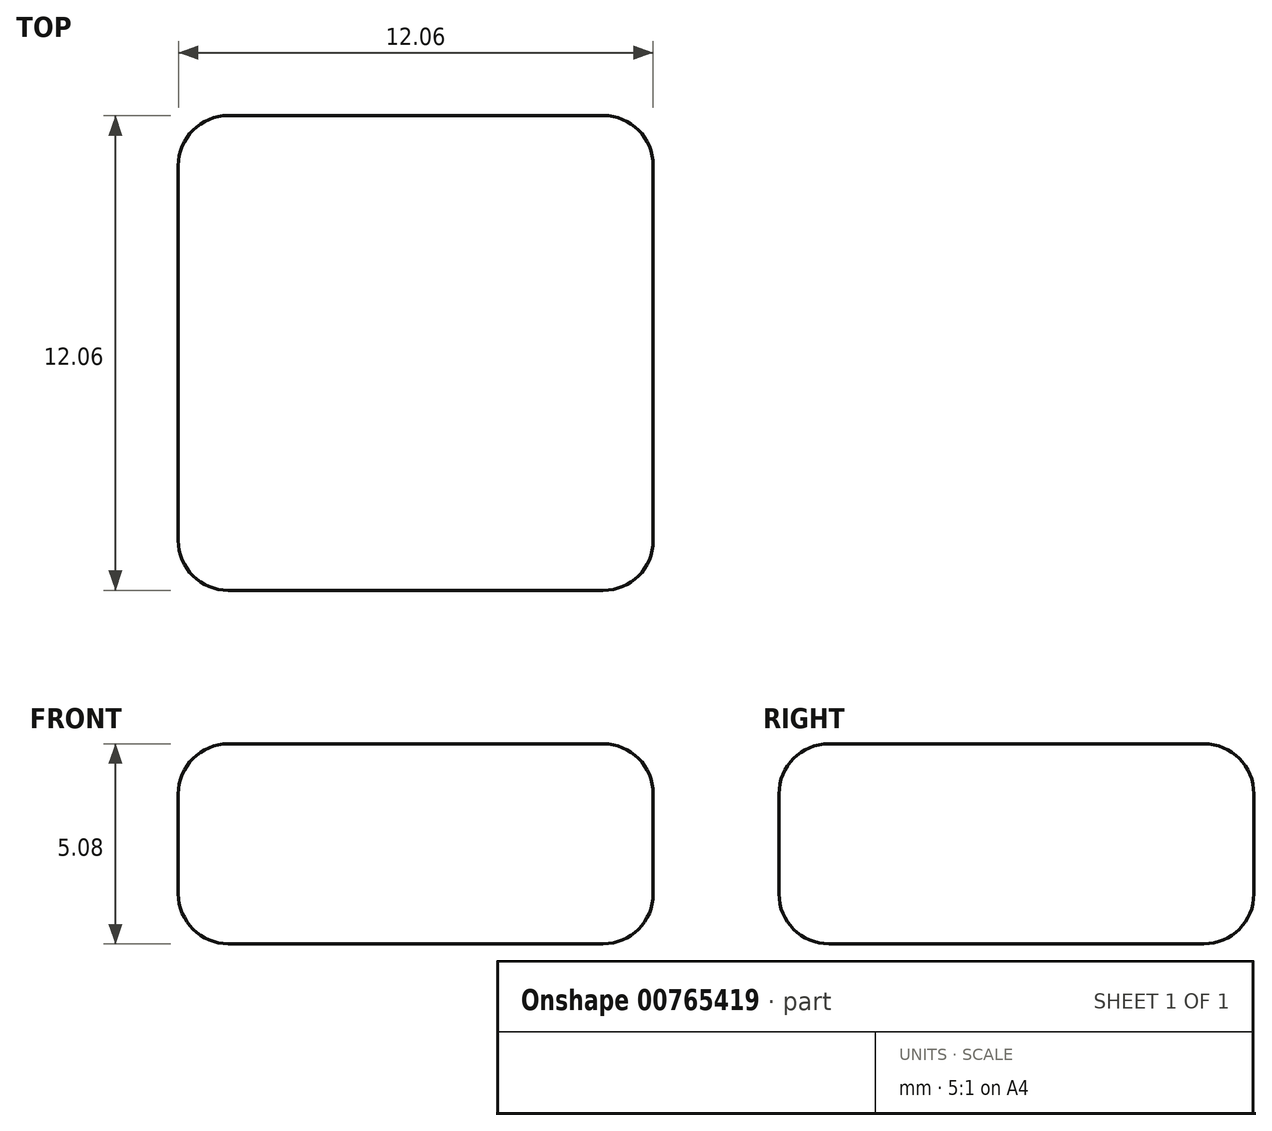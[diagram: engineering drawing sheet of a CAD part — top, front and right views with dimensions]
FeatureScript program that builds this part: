
annotation { "Feature Type Name" : "Feature", "Feature Type Description" : "" }
export const myFeature = defineFeature(function(context is Context, id is Id, definition is map)
    precondition{}
    {
        {
            var Q0;
            Q0=qCreatedBy(makeId("Top.planeOp"),FACE);
            var sketch = newSketch(context, id + "F0", { "sketchPlane" : qUnion([Q0])});
            skPoint(sketch, "E0", {"position": v(0, 0) * mm});
            skLineSegment(sketch, "E1.bottom", {"start": v(4.76, 6.03) * mm, "end": v(-4.76, 6.03) * mm});
            skLineSegment(sketch, "E1.top", {"start": v(4.76, -6.03) * mm, "end": v(-4.76, -6.03) * mm});
            skLineSegment(sketch, "E1.left", {"start": v(6.03, 4.76) * mm, "end": v(6.03, -4.76) * mm});
            skLineSegment(sketch, "E1.right", {"start": v(-6.03, 4.76) * mm, "end": v(-6.03, -4.76) * mm});
            skPoint(sketch, "E2.visualSharp", {"position": v(-6.03, 6.03) * mm});
            skArc(sketch, "E2.filletArc", {"start": v(-4.76, 6.03) * mm, "mid": v(-5.66, 5.66) * mm, "end": v(-6.03, 4.76) * mm});
            skPoint(sketch, "E3.visualSharp", {"position": v(-6.03, -6.03) * mm});
            skArc(sketch, "E3.filletArc", {"start": v(-6.03, -4.76) * mm, "mid": v(-5.66, -5.66) * mm, "end": v(-4.76, -6.03) * mm});
            skPoint(sketch, "E4.visualSharp", {"position": v(6.03, -6.03) * mm});
            skArc(sketch, "E4.filletArc", {"start": v(4.76, -6.03) * mm, "mid": v(5.66, -5.66) * mm, "end": v(6.03, -4.76) * mm});
            skPoint(sketch, "E5.visualSharp", {"position": v(6.03, 6.03) * mm});
            skArc(sketch, "E5.filletArc", {"start": v(6.03, 4.76) * mm, "mid": v(5.66, 5.66) * mm, "end": v(4.76, 6.03) * mm});
            skSolve(sketch);
        }
        {
            var Q0;
            Q0=makeQuery(id+"F0.imprint","IMPRINT",FACE,{"disambiguationData":[TD([[makeQuery(id+"F0.imprint","IMPRINT",EDGE,{"derivedFrom":sQuery(id+"F0.wireOp",EDGE,"E1.bottom")}),1.0]])]});
            extrude(context, id + "F1", {"entities" : qUnion([Q0]), "depth" : 5.08 * mm, "offsetDistance" : 25.4 * mm});
        }
        {
            var Q0;
            Q0=makeQuery(id+"F1.opExtrude","CAP_EDGE",EDGE,{"disambiguationData":[OSD([sQuery(id+"F0.wireOp",EDGE,"E1.top")])],"isStart":false});
            var Q1;
            Q1=makeQuery(id+"F1.opExtrude","CAP_EDGE",EDGE,{"disambiguationData":[OSD([sQuery(id+"F0.wireOp",EDGE,"E1.top")])],"isStart":true});
            fillet(context, id + "F2", {"entities" : qUnion([Q0, Q1]), "radius" : 1.27 * mm, "tangentPropagation" : true, "allowEdgeOverflow" : false});
        }
    });
